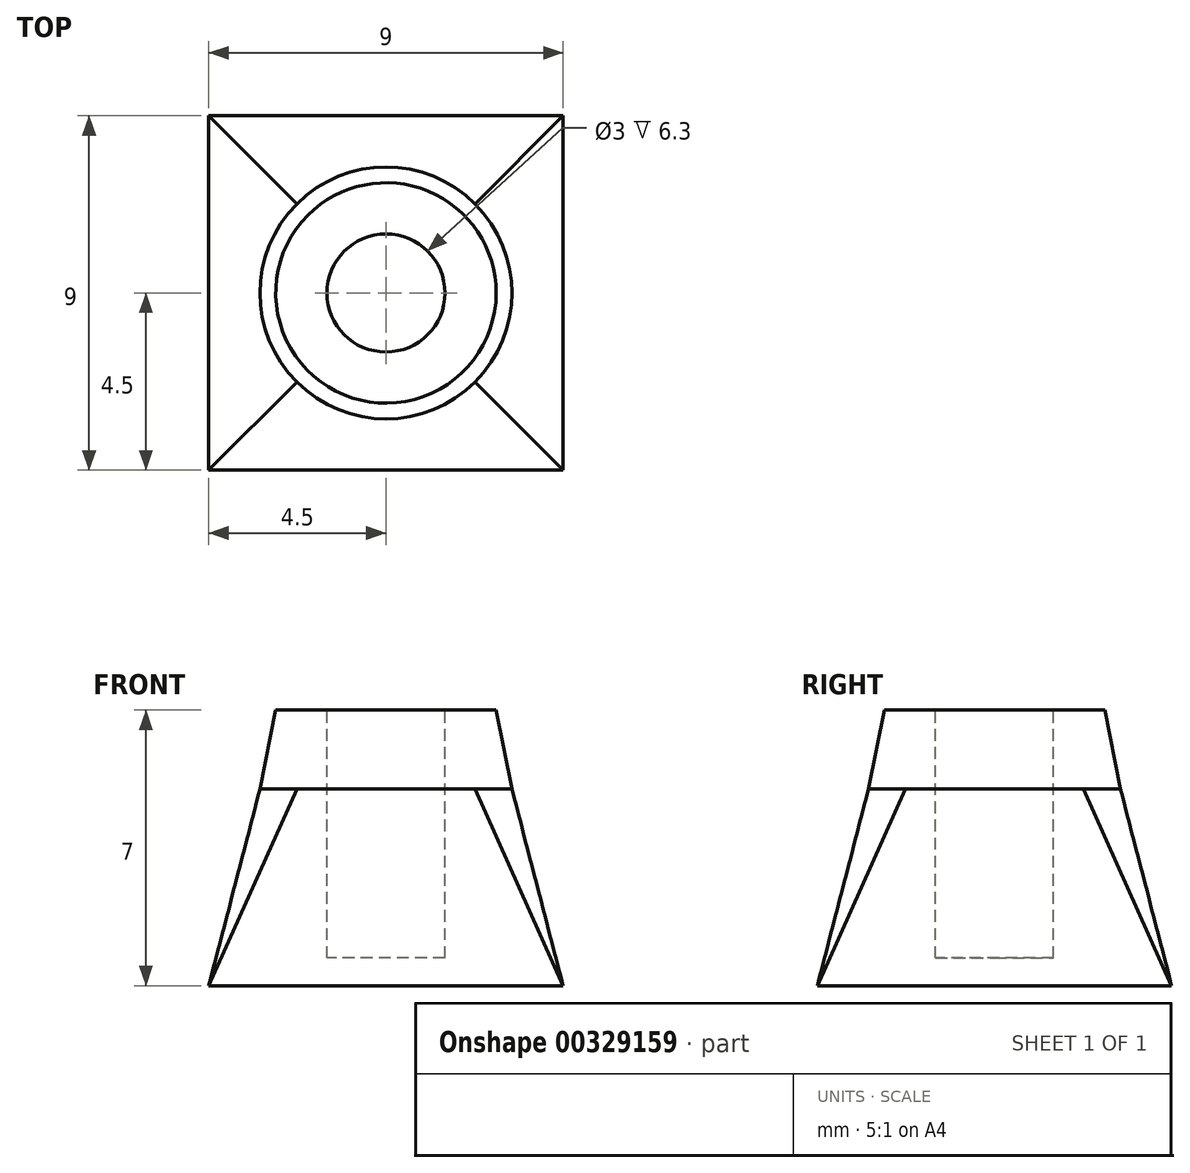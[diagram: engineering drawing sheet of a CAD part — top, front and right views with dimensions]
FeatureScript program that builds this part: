
annotation { "Feature Type Name" : "Feature", "Feature Type Description" : "" }
export const myFeature = defineFeature(function(context is Context, id is Id, definition is map)
    precondition{}
    {
        {
            var Q0;
            Q0=qCreatedBy(makeId("Top.planeOp"),FACE);
            var sketch = newSketch(context, id + "F0", { "sketchPlane" : qUnion([Q0])});
            skCircle(sketch, "E0", {"center": v(0, 0) * mm, "radius": 3.2 * mm});
            skSolve(sketch);
        }
        {
            var Q0;
            Q0=qCreatedBy(makeId("Top.planeOp"),FACE);
            cPlane(context, id + "F1", {"entities" : qUnion([Q0]), "cplaneType" : CPlaneType.OFFSET, "offset" : 5 * mm, "oppositeDirection" : true, "width" : 150 * mm, "height" : 150 * mm});
        }
        {
            var Q0;
            Q0=qCreatedBy(id+"F1.planeOp",FACE);
            var sketch = newSketch(context, id + "F2", { "sketchPlane" : qUnion([Q0])});
            skLineSegment(sketch, "E1.bottom", {"start": v(-4.5, -4.5) * mm, "end": v(4.5, -4.5) * mm});
            skLineSegment(sketch, "E1.top", {"start": v(-4.5, 4.5) * mm, "end": v(4.5, 4.5) * mm});
            skLineSegment(sketch, "E1.left", {"start": v(-4.5, -4.5) * mm, "end": v(-4.5, 4.5) * mm});
            skLineSegment(sketch, "E1.right", {"start": v(4.5, -4.5) * mm, "end": v(4.5, 4.5) * mm});
            skPoint(sketch, "E2", {"position": v(-4.5, 0) * mm});
            skPoint(sketch, "E3", {"position": v(0, 4.5) * mm});
            skSolve(sketch);
        }
        {
            var Q0;
            Q0=makeQuery(id+"F2.imprint","IMPRINT",FACE,{"disambiguationData":[TD([[makeQuery(id+"F2.imprint","IMPRINT",EDGE,{"derivedFrom":sQuery(id+"F2.wireOp",EDGE,"E1.bottom")}),1.0]])]});
            var Q1;
            Q1=makeQuery(id+"F0.imprint","IMPRINT",FACE,{"disambiguationData":[TD([[makeQuery(id+"F0.imprint","IMPRINT",EDGE,{"derivedFrom":sQuery(id+"F0.wireOp",EDGE,"E0")}),1.0]])]});
            loft(context, id + "F3", {"sheetProfilesArray" : [{ "sheetProfileEntities" : qUnion([Q0]) }, { "sheetProfileEntities" : qUnion([Q1]) }]});
        }
        {
            var Q0;
            Q0=qCreatedBy(makeId("Top.planeOp"),FACE);
            cPlane(context, id + "F4", {"entities" : qUnion([Q0]), "cplaneType" : CPlaneType.OFFSET, "offset" : 2 * mm, "width" : 150 * mm, "height" : 150 * mm});
        }
        {
            var Q0;
            Q0=qCreatedBy(id+"F4.planeOp",FACE);
            var sketch = newSketch(context, id + "F5", { "sketchPlane" : qUnion([Q0])});
            skCircle(sketch, "E4", {"center": v(0, 0) * mm, "radius": 2.8 * mm});
            skSolve(sketch);
        }
        {
            var Q1;
            Q1=makeQuery(id+"F0.imprint","IMPRINT",FACE,{"disambiguationData":[TD([[makeQuery(id+"F0.imprint","IMPRINT",EDGE,{"derivedFrom":sQuery(id+"F0.wireOp",EDGE,"E0")}),1.0]])]});
            var Q2;
            Q2=makeQuery(id+"F5.imprint","IMPRINT",FACE,{"disambiguationData":[TD([[makeQuery(id+"F5.imprint","IMPRINT",EDGE,{"derivedFrom":sQuery(id+"F5.wireOp",EDGE,"E4")}),1.0]])]});
            loft(context, id + "F6", {"operationType" : NewBodyOperationType.ADD, "sheetProfilesArray" : [{ "sheetProfileEntities" : qUnion([Q1]) }, { "sheetProfileEntities" : qUnion([Q2]) }]});
        }
        {
            var Q0;
            Q0=qCreatedBy(id+"F4.planeOp",FACE);
            var sketch = newSketch(context, id + "F7", { "sketchPlane" : qUnion([Q0])});
            skCircle(sketch, "E5", {"center": v(0, 0) * mm, "radius": 1.5 * mm});
            skSolve(sketch);
        }
        {
            var Q0;
            Q0=makeQuery(id+"F7.imprint","IMPRINT",FACE,{"disambiguationData":[TD([[makeQuery(id+"F7.imprint","IMPRINT",EDGE,{"derivedFrom":sQuery(id+"F7.wireOp",EDGE,"E5")}),1.0]])]});
            extrude(context, id + "F8", {"entities" : qUnion([Q0]), "operationType" : NewBodyOperationType.REMOVE, "oppositeDirection" : true, "depth" : 6.3 * mm});
        }
    });
